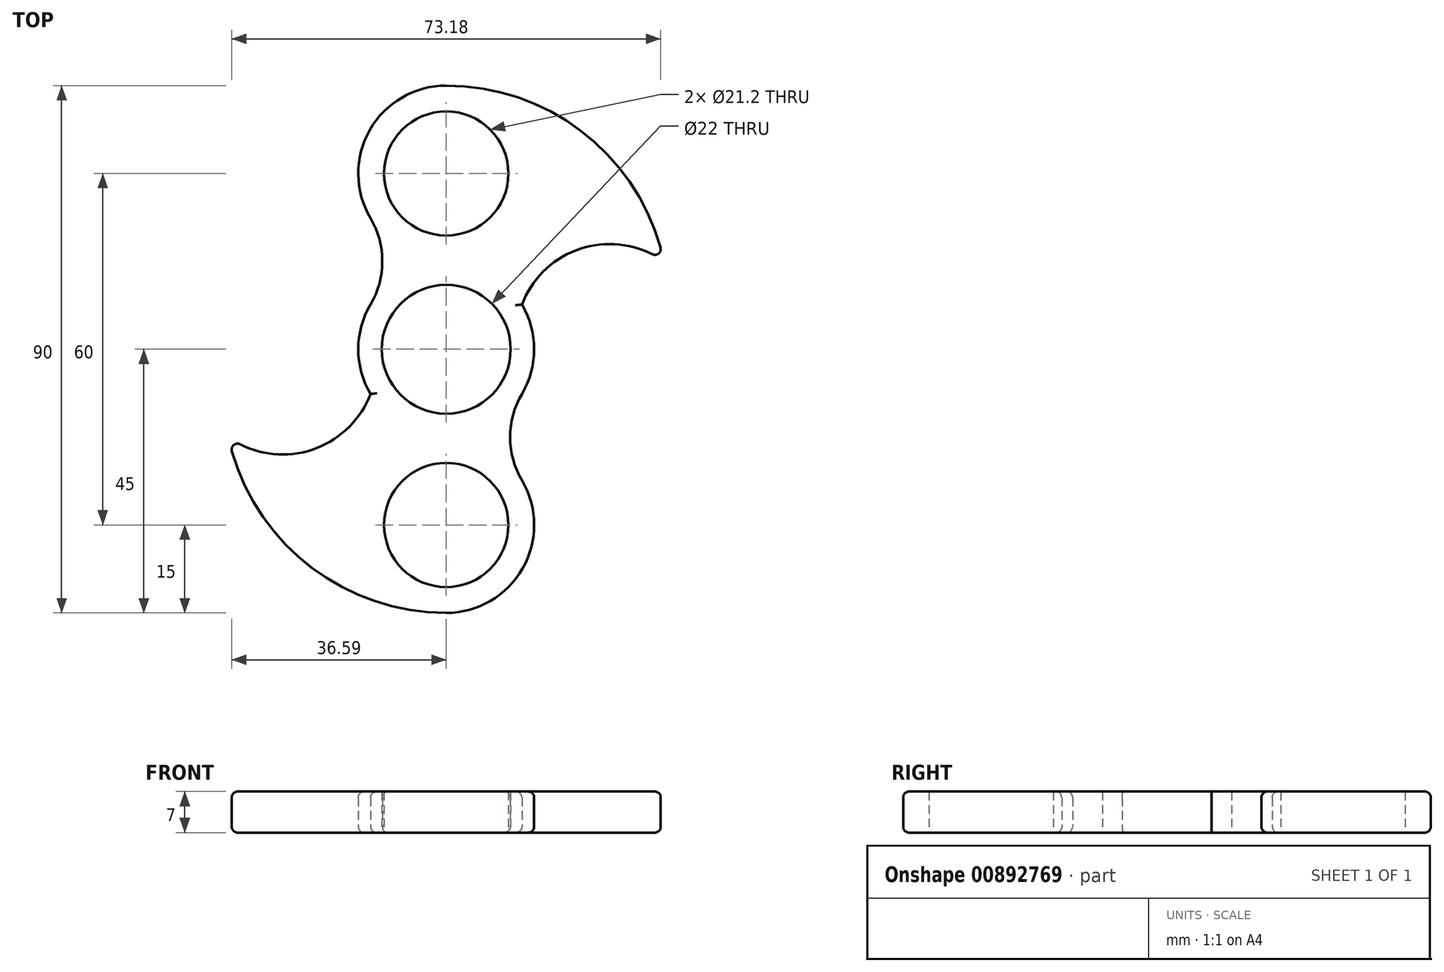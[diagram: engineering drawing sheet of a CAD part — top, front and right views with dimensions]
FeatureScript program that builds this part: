
annotation { "Feature Type Name" : "Feature", "Feature Type Description" : "" }
export const myFeature = defineFeature(function(context is Context, id is Id, definition is map)
    precondition{}
    {
        {
            var Q0;
            Q0=qCreatedBy(makeId("Top.planeOp"),FACE);
            var sketch = newSketch(context, id + "F0", { "sketchPlane" : qUnion([Q0])});
            skArc(sketch, "E0", {"start": v(-12.92, 7.63) * mm, "mid": v(-15, 0) * mm, "end": v(-12.92, -7.63) * mm});
            skArc(sketch, "E1", {"start": v(12.92, 22.37) * mm, "mid": v(0, 45) * mm, "end": v(-12.92, 22.37) * mm});
            skArc(sketch, "E2", {"start": v(-12.92, -22.37) * mm, "mid": v(0, -45) * mm, "end": v(12.92, -22.37) * mm});
            skArc(sketch, "E3", {"start": v(-12.92, 7.63) * mm, "mid": v(-10.9, 15) * mm, "end": v(-12.92, 22.37) * mm});
            skArc(sketch, "E4", {"start": v(-12.92, -22.37) * mm, "mid": v(-10.9, -15) * mm, "end": v(-12.92, -7.63) * mm});
            skArc(sketch, "E5", {"start": v(12.92, 22.37) * mm, "mid": v(10.9, 15) * mm, "end": v(12.92, 7.63) * mm});
            skArc(sketch, "E6", {"start": v(12.92, -7.63) * mm, "mid": v(10.9, -15) * mm, "end": v(12.92, -22.37) * mm});
            skArc(sketch, "E7.trimOffspring", {"start": v(12.92, -7.63) * mm, "mid": v(15, 0) * mm, "end": v(12.92, 7.63) * mm});
            skArc(sketch, "E8", {"start": v(-36.55, -17.38) * mm, "mid": v(-22.9, -37.32) * mm, "end": v(0, -45) * mm});
            skArc(sketch, "E9", {"start": v(-35.14, -16.22) * mm, "mid": v(-22.1, -16.88) * mm, "end": v(-12.92, -7.63) * mm});
            skArc(sketch, "E10", {"start": v(36.55, 17.38) * mm, "mid": v(22.9, 37.32) * mm, "end": v(0, 45) * mm});
            skArc(sketch, "E11", {"start": v(35.14, 16.22) * mm, "mid": v(22.1, 16.88) * mm, "end": v(12.92, 7.63) * mm});
            skPoint(sketch, "E12.visualSharp", {"position": v(37.15, 15) * mm});
            skArc(sketch, "E12.filletArc", {"start": v(35.14, 16.22) * mm, "mid": v(36.23, 16.34) * mm, "end": v(36.55, 17.38) * mm});
            skPoint(sketch, "E13.visualSharp", {"position": v(-37.15, -15) * mm});
            skArc(sketch, "E13.filletArc", {"start": v(-35.14, -16.22) * mm, "mid": v(-36.23, -16.34) * mm, "end": v(-36.55, -17.38) * mm});
            skSolve(sketch);
        }
        {
            var Q0;
            Q0=makeQuery(id+"F0.imprint","IMPRINT",FACE,{"disambiguationData":[TD([[makeQuery(id+"F0.imprint","IMPRINT",EDGE,{"derivedFrom":sQuery(id+"F0.wireOp",EDGE,"E0")}),1.0]])]});
            var Q1;
            {var subQ1=sQuery(id+"F0.wireOp",EDGE,"E5");Q1=makeQuery(id+"F0.imprint","IMPRINT",FACE,{"disambiguationData":[TD([[makeQuery(id+"F0.imprint","IMPRINT",EDGE,{"derivedFrom":subQ1}),1.0]])]});}
            var Q2;
            {var subQ1=sQuery(id+"F0.wireOp",EDGE,"E4");Q2=makeQuery(id+"F0.imprint","IMPRINT",FACE,{"disambiguationData":[TD([[makeQuery(id+"F0.imprint","IMPRINT",EDGE,{"derivedFrom":subQ1}),1.0]])]});}
            extrude(context, id + "F1", {"entities" : qUnion([Q0, Q1, Q2]), "depth" : 7 * mm, "offsetDistance" : 25 * mm});
        }
        {
            var Q0;
            Q0=makeQuery(id+"F1.opExtrude","CAP_EDGE",EDGE,{"disambiguationData":[OSD([sQuery(id+"F0.wireOp",EDGE,"E10")])],"isStart":false});
            var Q1;
            Q1=makeQuery(id+"F1.opExtrude","CAP_EDGE",EDGE,{"disambiguationData":[OSD([sQuery(id+"F0.wireOp",EDGE,"E8")])],"isStart":false});
            var Q2;
            Q2=makeQuery(id+"F1.opExtrude","CAP_EDGE",EDGE,{"disambiguationData":[OSD([sQuery(id+"F0.wireOp",EDGE,"E10")])],"isStart":true});
            var Q3;
            Q3=makeQuery(id+"F1.opExtrude","CAP_EDGE",EDGE,{"disambiguationData":[OSD([sQuery(id+"F0.wireOp",EDGE,"E8")])],"isStart":true});
            fillet(context, id + "F2", {"entities" : qUnion([Q0, Q1, Q2, Q3]), "radius" : 1 * mm, "tangentPropagation" : true, "allowEdgeOverflow" : false});
        }
        {
            var Q0;
            Q0=sQuery(id+"F0.wireOp",VERTEX,"E0.center");
            var Q1;
            Q1=makeQuery(id+"F1.opExtrude","SWEPT_BODY",BODY,{"disambiguationData":[OSD([sQuery(id+"F0.wireOp",EDGE,"E0"),sQuery(id+"F0.wireOp",EDGE,"E1"),sQuery(id+"F0.wireOp",EDGE,"E2"),sQuery(id+"F0.wireOp",EDGE,"E3"),sQuery(id+"F0.wireOp",EDGE,"E6"),sQuery(id+"F0.wireOp",EDGE,"E7.trimOffspring"),sQuery(id+"F0.wireOp",EDGE,"E8"),sQuery(id+"F0.wireOp",EDGE,"E9"),sQuery(id+"F0.wireOp",EDGE,"E10"),sQuery(id+"F0.wireOp",EDGE,"E11"),sQuery(id+"F0.wireOp",EDGE,"E12.filletArc"),sQuery(id+"F0.wireOp",EDGE,"E13.filletArc")])]});
            hole(context, id + "F3", {"style" : HoleStyle.SIMPLE, "endStyle" : HoleEndStyle.THROUGH, "oppositeDirection" : true, "holeDiameter" : 22 * mm, "majorDiameter" : 5 * mm, "isTappedThrough" : true, "tappedDepth" : 12 * mm, "tapClearance" : 3, "locations" : qUnion([Q0]), "scope" : qUnion([Q1])});
        }
        {
            var Q0;
            Q0=sQuery(id+"F0.wireOp",VERTEX,"E1.center");
            var Q1;
            Q1=sQuery(id+"F0.wireOp",VERTEX,"E2.center");
            var Q2;
            Q2=makeQuery(id+"F1.opExtrude","SWEPT_BODY",BODY,{"disambiguationData":[OSD([sQuery(id+"F0.wireOp",EDGE,"E0"),sQuery(id+"F0.wireOp",EDGE,"E1"),sQuery(id+"F0.wireOp",EDGE,"E2"),sQuery(id+"F0.wireOp",EDGE,"E3"),sQuery(id+"F0.wireOp",EDGE,"E6"),sQuery(id+"F0.wireOp",EDGE,"E7.trimOffspring"),sQuery(id+"F0.wireOp",EDGE,"E8"),sQuery(id+"F0.wireOp",EDGE,"E9"),sQuery(id+"F0.wireOp",EDGE,"E10"),sQuery(id+"F0.wireOp",EDGE,"E11"),sQuery(id+"F0.wireOp",EDGE,"E12.filletArc"),sQuery(id+"F0.wireOp",EDGE,"E13.filletArc")])]});
            hole(context, id + "F4", {"style" : HoleStyle.SIMPLE, "endStyle" : HoleEndStyle.THROUGH, "oppositeDirection" : true, "holeDiameter" : 21.2 * mm, "majorDiameter" : 5 * mm, "isTappedThrough" : true, "tappedDepth" : 12 * mm, "tapClearance" : 3, "locations" : qUnion([Q0, Q1]), "scope" : qUnion([Q2])});
        }
    });
